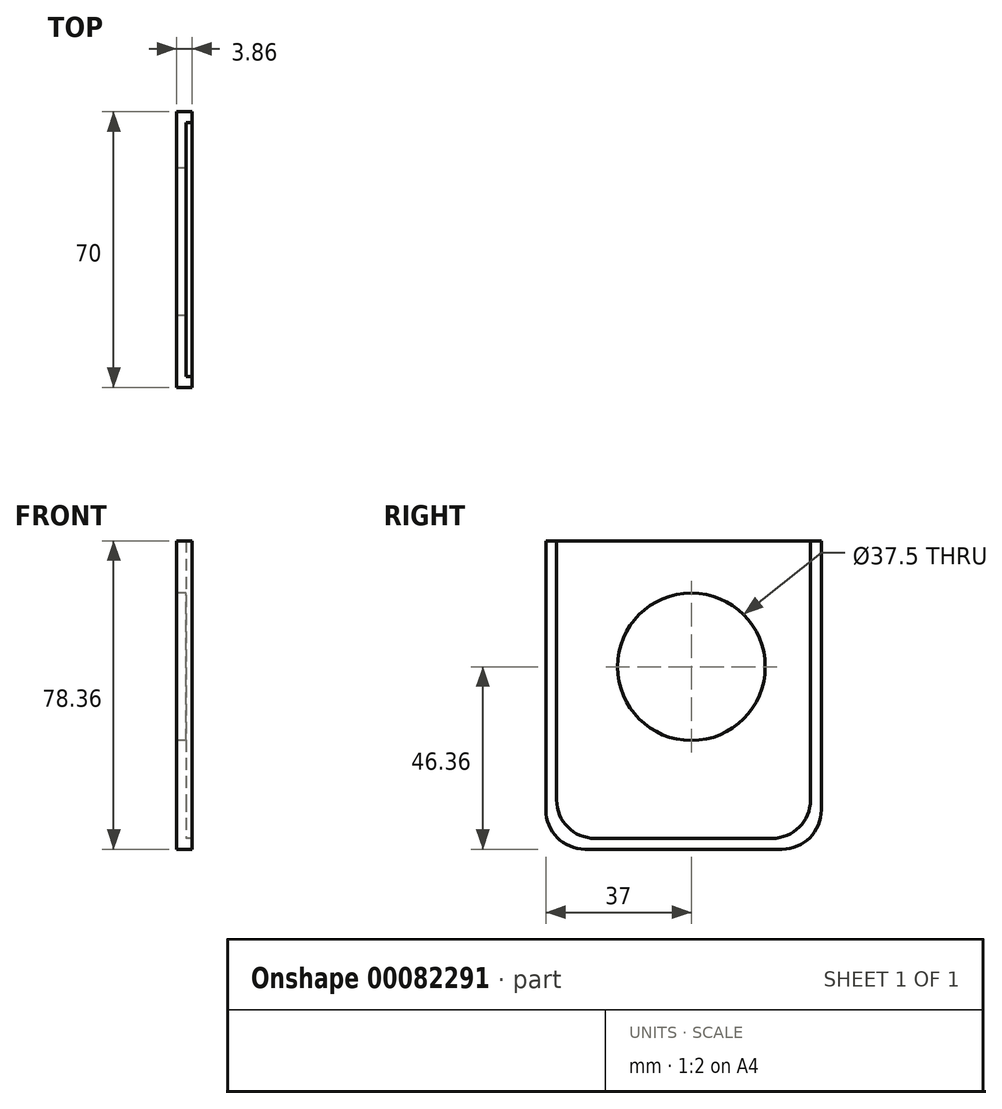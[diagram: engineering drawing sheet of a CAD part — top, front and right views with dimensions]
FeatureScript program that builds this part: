
annotation { "Feature Type Name" : "Feature", "Feature Type Description" : "" }
export const myFeature = defineFeature(function(context is Context, id is Id, definition is map)
    precondition{}
    {
        {
            var Q0;
            Q0=qCreatedBy(makeId("Right.planeOp"),FACE);
            var sketch = newSketch(context, id + "F0", { "sketchPlane" : qUnion([Q0])});
            skLineSegment(sketch, "E0", {"start": v(-27.5, 35) * mm, "end": v(-27.5, -30.86) * mm});
            skLineSegment(sketch, "E1", {"start": v(27.5, 35) * mm, "end": v(27.5, -30.86) * mm});
            skLineSegment(sketch, "E2", {"start": v(-22.5, -35.86) * mm, "end": v(22.5, -35.86) * mm});
            skPoint(sketch, "E3.orphan", {"position": v(-27.5, -21.94) * mm});
            skPoint(sketch, "E4.orphan", {"position": v(27.5, -21.94) * mm});
            skPoint(sketch, "E5.visualSharp", {"position": v(-27.5, -35.86) * mm});
            skArc(sketch, "E5.filletArc", {"start": v(-27.5, -30.86) * mm, "mid": v(-26.04, -34.4) * mm, "end": v(-22.5, -35.86) * mm});
            skPoint(sketch, "E6.visualSharp", {"position": v(27.5, -35.86) * mm});
            skArc(sketch, "E6.filletArc", {"start": v(22.5, -35.86) * mm, "mid": v(26.04, -34.4) * mm, "end": v(27.5, -30.86) * mm});
            skPoint(sketch, "E7.orphan", {"position": v(-27.5, 53.27) * mm});
            skPoint(sketch, "E8.orphan", {"position": v(27.5, 53.27) * mm});
            skLineSegment(sketch, "E9", {"start": v(-35, 35) * mm, "end": v(-35, -33.36) * mm});
            skLineSegment(sketch, "E10", {"start": v(-25, -43.36) * mm, "end": v(25, -43.36) * mm});
            skLineSegment(sketch, "E11", {"start": v(35, -33.36) * mm, "end": v(35, 35) * mm});
            skArc(sketch, "E12.filletArc", {"start": v(-35, -33.36) * mm, "mid": v(-32.07, -40.43) * mm, "end": v(-25, -43.36) * mm});
            skArc(sketch, "E13.filletArc", {"start": v(25, -43.36) * mm, "mid": v(32.07, -40.43) * mm, "end": v(35, -33.36) * mm});
            skLineSegment(sketch, "E14", {"start": v(35, 35) * mm, "end": v(-35, 35) * mm});
            skCircle(sketch, "E15", {"center": v(2, 3) * mm, "radius": 18.75 * mm});
            skSolve(sketch);
        }
        {
            var Q0;
            {var subQ2=sQuery(id+"F0.wireOp",EDGE,"E0");Q0=makeQuery(id+"F0.imprint","IMPRINT",FACE,{"disambiguationData":[TD([[makeQuery(id+"F0.imprint","IMPRINT",EDGE,{"derivedFrom":subQ2}),-1.0]])]});}
            extrude(context, id + "F1", {"entities" : qUnion([Q0]), "depth" : 7.5 * mm, "offsetDistance" : 25 * mm});
        }
        {
            var Q0;
            {var subQ0=sQuery(id+"F0.wireOp",EDGE,"E14");Q0=makeQuery(id+"F1.opExtrude","SWEPT_FACE",FACE,{"disambiguationData":[OSD([subQ0]),TDD([makeQuery(id+"F0.imprint","IMPRINT",EDGE,{"disambiguationData":[TD([[makeQuery(id+"F0.imprint","INTERSECT",VERTEX,{"derivedFrom":[sQuery(id+"F0.wireOp",EDGE,"E1"),subQ0]}),1.0]])],"derivedFrom":subQ0})])]});}
            var sketch = newSketch(context, id + "F2", { "sketchPlane" : qUnion([Q0])});
            skLineSegment(sketch, "E16.bottom", {"start": v(4.98, 27.5) * mm, "end": v(2.38, 27.5) * mm});
            skLineSegment(sketch, "E16.top", {"start": v(4.97, 32.25) * mm, "end": v(2.37, 32.25) * mm});
            skLineSegment(sketch, "E16.left", {"start": v(4.98, 27.5) * mm, "end": v(4.97, 32.25) * mm});
            skLineSegment(sketch, "E16.right", {"start": v(2.38, 27.5) * mm, "end": v(2.37, 32.25) * mm});
            skSolve(sketch);
        }
        {
            var Q0;
            Q0=makeQuery(id+"F2.imprint","IMPRINT",FACE,{"disambiguationData":[TD([[makeQuery(id+"F2.imprint","IMPRINT",EDGE,{"derivedFrom":sQuery(id+"F2.wireOp",EDGE,"E16.bottom")}),-1.0]])]});
            var Q1;
            Q1=sQuery(id+"F0.wireOp",EDGE,"E1");
            var Q2;
            Q2=sQuery(id+"F0.wireOp",EDGE,"E6.filletArc");
            var Q3;
            Q3=sQuery(id+"F0.wireOp",EDGE,"E2");
            var Q4;
            Q4=sQuery(id+"F0.wireOp",EDGE,"E5.filletArc");
            var Q5;
            Q5=sQuery(id+"F0.wireOp",EDGE,"E0");
            sweep(context, id + "F3", {"operationType" : NewBodyOperationType.REMOVE, "profiles" : qUnion([Q0]), "path" : qUnion([Q1, Q2, Q3, Q4, Q5])});
        }
        {
            var Q0;
            {var subQ2=sQuery(id+"F0.wireOp",EDGE,"E0");Q0=makeQuery(id+"F0.imprint","IMPRINT",FACE,{"disambiguationData":[TD([[makeQuery(id+"F0.imprint","IMPRINT",EDGE,{"derivedFrom":subQ2}),1.0]])]});}
            var Q1;
            Q1=makeQuery(id+"F0.imprint","IMPRINT",FACE,{"disambiguationData":[TD([[makeQuery(id+"F0.imprint","IMPRINT",EDGE,{"derivedFrom":sQuery(id+"F0.wireOp",EDGE,"RalXa7Zk-iRiR-DEGu-MVaw-sS2nsxJwCIpq")}),-1.0]])]});
            var Q2;
            Q2=makeQuery(id+"F0.imprint","IMPRINT",FACE,{"disambiguationData":[TD([[makeQuery(id+"F0.imprint","IMPRINT",EDGE,{"derivedFrom":sQuery(id+"F0.wireOp",EDGE,"RalXa7Zk-iRiR-DEGu-MVaw-sS2nsxJwCIpq")}),1.0]])]});
            var Q3;
            Q3=makeQuery(id+"F0.imprint","IMPRINT",FACE,{"disambiguationData":[TD([[makeQuery(id+"F0.imprint","IMPRINT",EDGE,{"derivedFrom":sQuery(id+"F0.wireOp",EDGE,"85QicEso-iMtD-wqBT-e6sD-r58lY0pxuzTS")}),1.0]])]});
            extrude(context, id + "F4", {"entities" : qUnion([Q0, Q1, Q2, Q3]), "operationType" : NewBodyOperationType.ADD, "depth" : 2.38 * mm, "offsetDistance" : 25 * mm});
        }
        {
            var Q0;
            Q0=qCreatedBy(makeId("Top.planeOp"),FACE);
            cPlane(context, id + "F5", {"entities" : qUnion([Q0]), "cplaneType" : CPlaneType.OFFSET, "offset" : 1 * mm, "width" : 150 * mm, "height" : 150 * mm});
        }
        {
            var Q0;
            Q0=qCreatedBy(id+"F5.planeOp",FACE);
            var sketch = newSketch(context, id + "F6", { "sketchPlane" : qUnion([Q0])});
            skLineSegment(sketch, "E17", {"start": v(0, 25) * mm, "end": v(-22.6, 35) * mm});
            skLineSegment(sketch, "E18", {"start": v(-22.6, 35) * mm, "end": v(-22.6, 32) * mm});
            skLineSegment(sketch, "E19", {"start": v(-22.6, 32) * mm, "end": v(0, 22) * mm});
            skLineSegment(sketch, "E20", {"start": v(0, 22) * mm, "end": v(0, 25) * mm});
            skSolve(sketch);
        }
        {
            var Q0;
            Q0=makeQuery(id+"F6.imprint","IMPRINT",FACE,{"disambiguationData":[TD([[makeQuery(id+"F6.imprint","IMPRINT",EDGE,{"derivedFrom":sQuery(id+"F6.wireOp",EDGE,"E17")}),1.0]])]});
            var Q1;
            Q1=sQuery(id+"F0.wireOp",EDGE,"E15");
            revolve(context, id + "F7", {"operationType" : NewBodyOperationType.ADD, "surfaceOperationType" : NewSurfaceOperationType.NEW, "entities" : qUnion([Q0]), "axis" : qUnion([Q1]), "revolveType" : RevolveType.FULL});
        }
        {
            var Q0;
            {var subQ0=sQuery(id+"F0.wireOp",EDGE,"E0");var subQ1=sQuery(id+"F0.wireOp",EDGE,"E14");var subQ3=sQuery(id+"F0.wireOp",EDGE,"E1");Q0=makeQuery(id+"F3.boolean.opBoolean","SPLIT",EDGE,{"disambiguationData":[TD([makeQuery(id+"F3.opSweep","SWEPT_FACE",FACE,{"disambiguationData":[OSD([subQ3,sQuery(id+"F2.wireOp",EDGE,"E16.left")])]})])],"derivedFrom":makeQuery(id+"F1.opExtrude","SWEPT_EDGE",EDGE,{"disambiguationData":[OSD([subQ0,subQ1])]})});}
            var Q1;
            {var subQ0=sQuery(id+"F0.wireOp",EDGE,"E14");var subQ2=sQuery(id+"F0.wireOp",EDGE,"E1");Q1=makeQuery(id+"F3.boolean.opBoolean","SPLIT",EDGE,{"disambiguationData":[TD([makeQuery(id+"F3.opSweep","SWEPT_FACE",FACE,{"disambiguationData":[OSD([subQ2,sQuery(id+"F2.wireOp",EDGE,"E16.left")])]})])],"derivedFrom":makeQuery(id+"F1.opExtrude","SWEPT_EDGE",EDGE,{"disambiguationData":[OSD([subQ2,subQ0])]})});}
            fillet(context, id + "F8", {"entities" : qUnion([Q0, Q1]), "tangentPropagation" : true, "radius" : 4 * mm, "defaultsChanged" : false, "vertexSettings" : [], "allowEdgeOverflow" : false});
        }
        {
            var Q0;
            Q0=qCreatedBy(id+"F5.planeOp",FACE);
            var sketch = newSketch(context, id + "F9", { "sketchPlane" : qUnion([Q0])});
            skLineSegment(sketch, "E21.bottom", {"start": v(0, -42.7) * mm, "end": v(-29.16, -42.7) * mm});
            skLineSegment(sketch, "E21.top", {"start": v(0, 45.08) * mm, "end": v(-29.16, 45.08) * mm});
            skLineSegment(sketch, "E21.left", {"start": v(0, -42.7) * mm, "end": v(0, 45.08) * mm});
            skLineSegment(sketch, "E21.right", {"start": v(-29.16, -42.7) * mm, "end": v(-29.16, 45.08) * mm});
            skLineSegment(sketch, "E22.bottom", {"start": v(3.86, -42.7) * mm, "end": v(10.68, -42.7) * mm});
            skLineSegment(sketch, "E22.top", {"start": v(3.86, 45.08) * mm, "end": v(10.68, 45.08) * mm});
            skLineSegment(sketch, "E22.left", {"start": v(3.86, -42.7) * mm, "end": v(3.86, 45.08) * mm});
            skLineSegment(sketch, "E22.right", {"start": v(10.68, -42.7) * mm, "end": v(10.68, 45.08) * mm});
            skSolve(sketch);
        }
        {
            var Q0;
            Q0=makeQuery(id+"F9.imprint","IMPRINT",FACE,{"disambiguationData":[TD([[makeQuery(id+"F9.imprint","IMPRINT",EDGE,{"derivedFrom":sQuery(id+"F9.wireOp",EDGE,"E21.bottom")}),-1.0]])]});
            var Q1;
            Q1=makeQuery(id+"F9.imprint","IMPRINT",FACE,{"disambiguationData":[TD([[makeQuery(id+"F9.imprint","IMPRINT",EDGE,{"derivedFrom":sQuery(id+"F9.wireOp",EDGE,"E22.bottom")}),1.0]])]});
            extrude(context, id + "F10", {"entities" : qUnion([Q0, Q1]), "operationType" : NewBodyOperationType.REMOVE, "oppositeDirection" : true, "depth" : 120.2 * mm, "offsetDistance" : 25 * mm, "symmetric" : true});
        }
    });
